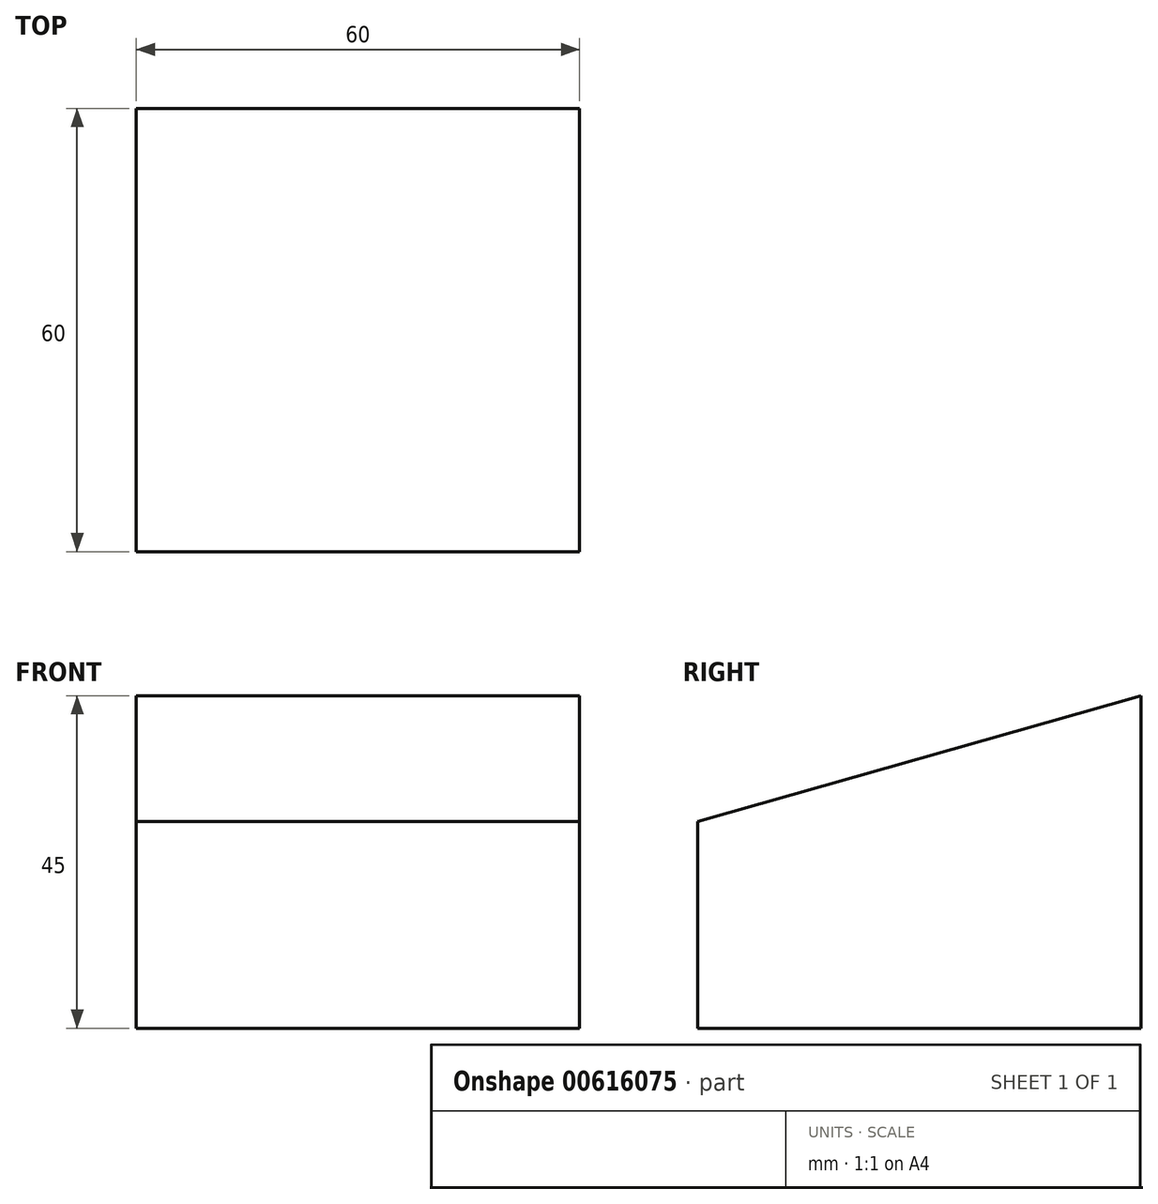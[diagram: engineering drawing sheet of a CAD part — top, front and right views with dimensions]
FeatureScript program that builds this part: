
annotation { "Feature Type Name" : "Feature", "Feature Type Description" : "" }
export const myFeature = defineFeature(function(context is Context, id is Id, definition is map)
    precondition{}
    {
        {
            var Q0;
            Q0=qCreatedBy(makeId("Right.planeOp"),FACE);
            var sketch = newSketch(context, id + "F0", { "sketchPlane" : qUnion([Q0])});
            skLineSegment(sketch, "E0", {"start": v(0, 0) * mm, "end": v(60, 0) * mm});
            skLineSegment(sketch, "E1", {"start": v(60, 0) * mm, "end": v(60, 45) * mm});
            skLineSegment(sketch, "E2", {"start": v(60, 45) * mm, "end": v(0, 28) * mm});
            skLineSegment(sketch, "E3", {"start": v(0, 0) * mm, "end": v(0, 28) * mm});
            skSolve(sketch);
        }
        {
            var Q0;
            Q0=makeQuery(id+"F0.imprint","IMPRINT",FACE,{"disambiguationData":[TD([[makeQuery(id+"F0.imprint","IMPRINT",EDGE,{"derivedFrom":sQuery(id+"F0.wireOp",EDGE,"E0")}),1.0]])]});
            extrude(context, id + "F1", {"entities" : qUnion([Q0]), "depth" : 60 * mm, "offsetDistance" : 25 * mm});
        }
    });
